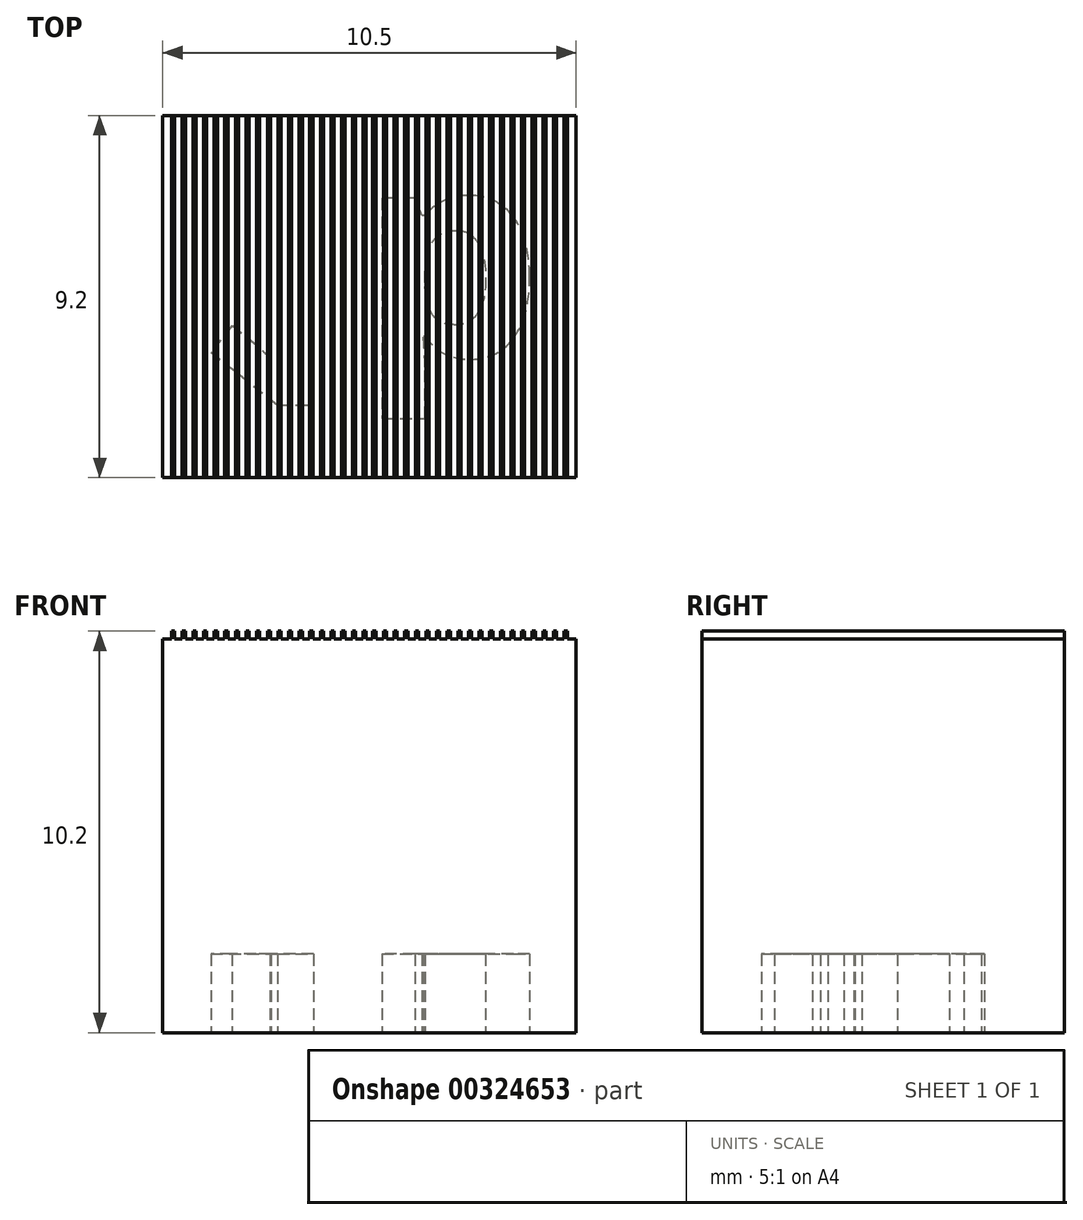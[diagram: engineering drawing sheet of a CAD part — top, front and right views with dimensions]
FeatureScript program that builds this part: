
annotation { "Feature Type Name" : "Feature", "Feature Type Description" : "" }
export const myFeature = defineFeature(function(context is Context, id is Id, definition is map)
    precondition{}
    {
        {
            assignVariable(context, id + "F0", {"name" : "h", "anyValue" : 10});
        }
        {
            assignVariable(context, id + "F1", {"name" : "gh", "anyValue" : 0.2});
        }
        {
            var Q0;
            Q0=qCreatedBy(makeId("Top.planeOp"),FACE);
            var sketch = newSketch(context, id + "F2", { "sketchPlane" : qUnion([Q0])});
            skLineSegment(sketch, "E0.bottom", {"start": v(5.25, 4.6) * mm, "end": v(-5.25, 4.6) * mm});
            skLineSegment(sketch, "E0.top", {"start": v(5.25, -4.6) * mm, "end": v(-5.25, -4.6) * mm});
            skLineSegment(sketch, "E0.left", {"start": v(5.25, 4.6) * mm, "end": v(5.25, -4.6) * mm});
            skLineSegment(sketch, "E0.right", {"start": v(-5.25, 4.6) * mm, "end": v(-5.25, -4.6) * mm});
            skPoint(sketch, "E0.middle", {"position": v(0, 0) * mm});
            skSolve(sketch);
        }
        {
            var Q0;
            Q0=qSketchRegion(id+"F2",true);
            extrude(context, id + "F3", {"entities" : qUnion([Q0]), "depth" : (getVariable(context, 'h')) * mm});
        }
        {
            var Q0;
            Q0=makeQuery(id+"F3.opExtrude","CAP_FACE",FACE,{"disambiguationData":[OSD([sQuery(id+"F2.wireOp",EDGE,"E0.bottom"),sQuery(id+"F2.wireOp",EDGE,"E0.top"),sQuery(id+"F2.wireOp",EDGE,"E0.left"),sQuery(id+"F2.wireOp",EDGE,"E0.right")])],"isStart":false});
            var sketch = newSketch(context, id + "F4", { "sketchPlane" : qUnion([Q0])});
            skLineSegment(sketch, "E1", {"start": v(0.08, 4.6) * mm, "end": v(0.09, -4.6) * mm});
            skLineSegment(sketch, "E2", {"start": v(-0.08, -4.6) * mm, "end": v(-0.09, 4.6) * mm, "construction": true});
            skLineSegment(sketch, "E3", {"start": v(0.17, -4.6) * mm, "end": v(0.16, 4.6) * mm});
            skLineSegment(sketch, "E4", {"start": v(0.09, 0) * mm, "end": v(-0.09, 0) * mm, "construction": true});
            skPoint(sketch, "E5", {"position": v(0, 0) * mm});
            skLineSegment(sketch, "E6", {"start": v(0.09, 4.6) * mm, "end": v(0.16, 4.6) * mm});
            skLineSegment(sketch, "E7", {"start": v(0.16, -4.6) * mm, "end": v(0.09, -4.6) * mm});
            skLineSegment(sketch, "E8.1.0.0", {"start": v(0.36, 4.6) * mm, "end": v(0.43, 4.6) * mm});
            skLineSegment(sketch, "E8.1.0.1", {"start": v(0.44, -4.6) * mm, "end": v(0.43, 4.6) * mm});
            skLineSegment(sketch, "E8.1.0.2", {"start": v(0.35, 4.6) * mm, "end": v(0.36, -4.6) * mm});
            skLineSegment(sketch, "E8.1.0.3", {"start": v(0.43, -4.6) * mm, "end": v(0.36, -4.6) * mm});
            skLineSegment(sketch, "E8.2.0.0", {"start": v(0.62, 4.6) * mm, "end": v(0.7, 4.6) * mm});
            skLineSegment(sketch, "E8.2.0.1", {"start": v(0.7, -4.6) * mm, "end": v(0.7, 4.6) * mm});
            skLineSegment(sketch, "E8.2.0.2", {"start": v(0.62, 4.6) * mm, "end": v(0.62, -4.6) * mm});
            skLineSegment(sketch, "E8.2.0.3", {"start": v(0.7, -4.6) * mm, "end": v(0.62, -4.6) * mm});
            skLineSegment(sketch, "E8.3.0.0", {"start": v(0.9, 4.6) * mm, "end": v(0.97, 4.6) * mm});
            skLineSegment(sketch, "E8.3.0.1", {"start": v(0.97, -4.6) * mm, "end": v(0.97, 4.6) * mm});
            skLineSegment(sketch, "E8.3.0.2", {"start": v(0.9, 4.6) * mm, "end": v(0.9, -4.6) * mm});
            skLineSegment(sketch, "E8.3.0.3", {"start": v(0.97, -4.6) * mm, "end": v(0.9, -4.6) * mm});
            skLineSegment(sketch, "E8.4.0.0", {"start": v(1.16, 4.6) * mm, "end": v(1.24, 4.6) * mm});
            skLineSegment(sketch, "E8.4.0.1", {"start": v(1.24, -4.6) * mm, "end": v(1.24, 4.6) * mm});
            skLineSegment(sketch, "E8.4.0.2", {"start": v(1.16, 4.6) * mm, "end": v(1.16, -4.6) * mm});
            skLineSegment(sketch, "E8.4.0.3", {"start": v(1.24, -4.6) * mm, "end": v(1.16, -4.6) * mm});
            skLineSegment(sketch, "E8.5.0.0", {"start": v(1.43, 4.6) * mm, "end": v(1.51, 4.6) * mm});
            skLineSegment(sketch, "E8.5.0.1", {"start": v(1.51, -4.6) * mm, "end": v(1.51, 4.6) * mm});
            skLineSegment(sketch, "E8.5.0.2", {"start": v(1.43, 4.6) * mm, "end": v(1.43, -4.6) * mm});
            skLineSegment(sketch, "E8.5.0.3", {"start": v(1.51, -4.6) * mm, "end": v(1.43, -4.6) * mm});
            skLineSegment(sketch, "E8.6.0.0", {"start": v(1.7, 4.6) * mm, "end": v(1.78, 4.6) * mm});
            skLineSegment(sketch, "E8.6.0.1", {"start": v(1.78, -4.6) * mm, "end": v(1.78, 4.6) * mm});
            skLineSegment(sketch, "E8.6.0.2", {"start": v(1.7, 4.6) * mm, "end": v(1.7, -4.6) * mm});
            skLineSegment(sketch, "E8.6.0.3", {"start": v(1.78, -4.6) * mm, "end": v(1.7, -4.6) * mm});
            skLineSegment(sketch, "E8.7.0.0", {"start": v(1.97, 4.6) * mm, "end": v(2.05, 4.6) * mm});
            skLineSegment(sketch, "E8.7.0.1", {"start": v(2.05, -4.6) * mm, "end": v(2.05, 4.6) * mm});
            skLineSegment(sketch, "E8.7.0.2", {"start": v(1.97, 4.6) * mm, "end": v(1.97, -4.6) * mm});
            skLineSegment(sketch, "E8.7.0.3", {"start": v(2.05, -4.6) * mm, "end": v(1.97, -4.6) * mm});
            skLineSegment(sketch, "E8.8.0.0", {"start": v(2.24, 4.6) * mm, "end": v(2.32, 4.6) * mm});
            skLineSegment(sketch, "E8.8.0.1", {"start": v(2.32, -4.6) * mm, "end": v(2.32, 4.6) * mm});
            skLineSegment(sketch, "E8.8.0.2", {"start": v(2.24, 4.6) * mm, "end": v(2.24, -4.6) * mm});
            skLineSegment(sketch, "E8.8.0.3", {"start": v(2.32, -4.6) * mm, "end": v(2.24, -4.6) * mm});
            skLineSegment(sketch, "E8.9.0.0", {"start": v(2.51, 4.6) * mm, "end": v(2.6, 4.6) * mm});
            skLineSegment(sketch, "E8.9.0.1", {"start": v(2.6, -4.6) * mm, "end": v(2.6, 4.6) * mm});
            skLineSegment(sketch, "E8.9.0.2", {"start": v(2.51, 4.6) * mm, "end": v(2.51, -4.6) * mm});
            skLineSegment(sketch, "E8.9.0.3", {"start": v(2.6, -4.6) * mm, "end": v(2.51, -4.6) * mm});
            skLineSegment(sketch, "E8.direction1", {"start": v(0.09, 4.6) * mm, "end": v(0.36, 4.6) * mm, "construction": true});
            skLineSegment(sketch, "E9.0.10.0", {"start": v(2.78, 4.6) * mm, "end": v(2.86, 4.6) * mm});
            skLineSegment(sketch, "E9.3.10.0", {"start": v(2.86, -4.6) * mm, "end": v(2.86, 4.6) * mm});
            skLineSegment(sketch, "E9.6.10.0", {"start": v(2.78, 4.6) * mm, "end": v(2.78, -4.6) * mm});
            skLineSegment(sketch, "E9.9.10.0", {"start": v(2.86, -4.6) * mm, "end": v(2.78, -4.6) * mm});
            skLineSegment(sketch, "E10.0.11.0", {"start": v(3.05, 4.6) * mm, "end": v(3.13, 4.6) * mm});
            skLineSegment(sketch, "E10.3.11.0", {"start": v(3.13, -4.6) * mm, "end": v(3.13, 4.6) * mm});
            skLineSegment(sketch, "E10.6.11.0", {"start": v(3.05, 4.6) * mm, "end": v(3.05, -4.6) * mm});
            skLineSegment(sketch, "E10.9.11.0", {"start": v(3.13, -4.6) * mm, "end": v(3.05, -4.6) * mm});
            skLineSegment(sketch, "E11.0.12.0", {"start": v(3.32, 4.6) * mm, "end": v(3.4, 4.6) * mm});
            skLineSegment(sketch, "E11.3.12.0", {"start": v(3.4, -4.6) * mm, "end": v(3.4, 4.6) * mm});
            skLineSegment(sketch, "E11.6.12.0", {"start": v(3.32, 4.6) * mm, "end": v(3.32, -4.6) * mm});
            skLineSegment(sketch, "E11.9.12.0", {"start": v(3.4, -4.6) * mm, "end": v(3.32, -4.6) * mm});
            skLineSegment(sketch, "E12.0.13.0", {"start": v(3.6, 4.6) * mm, "end": v(3.67, 4.6) * mm});
            skLineSegment(sketch, "E12.3.13.0", {"start": v(3.67, -4.6) * mm, "end": v(3.67, 4.6) * mm});
            skLineSegment(sketch, "E12.6.13.0", {"start": v(3.6, 4.6) * mm, "end": v(3.6, -4.6) * mm});
            skLineSegment(sketch, "E12.9.13.0", {"start": v(3.67, -4.6) * mm, "end": v(3.6, -4.6) * mm});
            skLineSegment(sketch, "E13.0.14.0", {"start": v(3.86, 4.6) * mm, "end": v(3.94, 4.6) * mm});
            skLineSegment(sketch, "E13.3.14.0", {"start": v(3.94, -4.6) * mm, "end": v(3.94, 4.6) * mm});
            skLineSegment(sketch, "E13.6.14.0", {"start": v(3.86, 4.6) * mm, "end": v(3.86, -4.6) * mm});
            skLineSegment(sketch, "E13.9.14.0", {"start": v(3.94, -4.6) * mm, "end": v(3.86, -4.6) * mm});
            skLineSegment(sketch, "E14.0.15.0", {"start": v(4.13, 4.6) * mm, "end": v(4.21, 4.6) * mm});
            skLineSegment(sketch, "E14.3.15.0", {"start": v(4.21, -4.6) * mm, "end": v(4.21, 4.6) * mm});
            skLineSegment(sketch, "E14.6.15.0", {"start": v(4.13, 4.6) * mm, "end": v(4.13, -4.6) * mm});
            skLineSegment(sketch, "E14.9.15.0", {"start": v(4.21, -4.6) * mm, "end": v(4.13, -4.6) * mm});
            skLineSegment(sketch, "E14.0.16.0", {"start": v(4.4, 4.6) * mm, "end": v(4.48, 4.6) * mm});
            skLineSegment(sketch, "E14.3.16.0", {"start": v(4.48, -4.6) * mm, "end": v(4.48, 4.6) * mm});
            skLineSegment(sketch, "E14.6.16.0", {"start": v(4.4, 4.6) * mm, "end": v(4.4, -4.6) * mm});
            skLineSegment(sketch, "E14.9.16.0", {"start": v(4.48, -4.6) * mm, "end": v(4.4, -4.6) * mm});
            skLineSegment(sketch, "E15.0.17.0", {"start": v(4.67, 4.6) * mm, "end": v(4.75, 4.6) * mm});
            skLineSegment(sketch, "E15.3.17.0", {"start": v(4.75, -4.6) * mm, "end": v(4.75, 4.6) * mm});
            skLineSegment(sketch, "E15.6.17.0", {"start": v(4.67, 4.6) * mm, "end": v(4.67, -4.6) * mm});
            skLineSegment(sketch, "E15.9.17.0", {"start": v(4.75, -4.6) * mm, "end": v(4.67, -4.6) * mm});
            skLineSegment(sketch, "E15.0.18.0", {"start": v(4.94, 4.6) * mm, "end": v(5.02, 4.6) * mm});
            skLineSegment(sketch, "E15.3.18.0", {"start": v(5.02, -4.6) * mm, "end": v(5.02, 4.6) * mm});
            skLineSegment(sketch, "E15.6.18.0", {"start": v(4.94, 4.6) * mm, "end": v(4.94, -4.6) * mm});
            skLineSegment(sketch, "E15.9.18.0", {"start": v(5.02, -4.6) * mm, "end": v(4.94, -4.6) * mm});
            skLineSegment(sketch, "E16.MirrorCS", {"start": v(-0.36, 4.6) * mm, "end": v(-0.43, 4.6) * mm});
            skLineSegment(sketch, "E17.MirrorCS", {"start": v(-0.09, 4.6) * mm, "end": v(-0.16, 4.6) * mm});
            skLineSegment(sketch, "E18.MirrorCS", {"start": v(-4.67, 4.6) * mm, "end": v(-4.75, 4.6) * mm});
            skLineSegment(sketch, "E19.MirrorCS", {"start": v(-2.6, -4.6) * mm, "end": v(-2.51, -4.6) * mm});
            skLineSegment(sketch, "E20.MirrorCS", {"start": v(-3.6, 4.6) * mm, "end": v(-3.67, 4.6) * mm});
            skLineSegment(sketch, "E21.MirrorCS", {"start": v(-1.7, 4.6) * mm, "end": v(-1.78, 4.6) * mm});
            skLineSegment(sketch, "E22.MirrorCS", {"start": v(-2.05, -4.6) * mm, "end": v(-1.97, -4.6) * mm});
            skLineSegment(sketch, "E23.MirrorCS", {"start": v(-1.51, -4.6) * mm, "end": v(-1.43, -4.6) * mm});
            skLineSegment(sketch, "E24.MirrorCS", {"start": v(-5.02, -4.6) * mm, "end": v(-4.94, -4.6) * mm});
            skLineSegment(sketch, "E25.MirrorCS", {"start": v(-3.32, 4.6) * mm, "end": v(-3.4, 4.6) * mm});
            skLineSegment(sketch, "E26.MirrorCS", {"start": v(-0.9, 4.6) * mm, "end": v(-0.97, 4.6) * mm});
            skLineSegment(sketch, "E27.MirrorCS", {"start": v(-1.97, 4.6) * mm, "end": v(-2.05, 4.6) * mm});
            skLineSegment(sketch, "E28.MirrorCS", {"start": v(-4.4, 4.6) * mm, "end": v(-4.48, 4.6) * mm});
            skLineSegment(sketch, "E29.MirrorCS", {"start": v(-0.16, -4.6) * mm, "end": v(-0.09, -4.6) * mm});
            skLineSegment(sketch, "E30.MirrorCS", {"start": v(-4.94, 4.6) * mm, "end": v(-5.02, 4.6) * mm});
            skLineSegment(sketch, "E31.MirrorCS", {"start": v(-2.78, 4.6) * mm, "end": v(-2.86, 4.6) * mm});
            skLineSegment(sketch, "E32.MirrorCS", {"start": v(-3.86, 4.6) * mm, "end": v(-3.94, 4.6) * mm});
            skLineSegment(sketch, "E33.MirrorCS", {"start": v(-3.13, -4.6) * mm, "end": v(-3.05, -4.6) * mm});
            skLineSegment(sketch, "E34.MirrorCS", {"start": v(-4.21, -4.6) * mm, "end": v(-4.13, -4.6) * mm});
            skLineSegment(sketch, "E35.MirrorCS", {"start": v(-1.16, 4.6) * mm, "end": v(-1.24, 4.6) * mm});
            skLineSegment(sketch, "E36.MirrorCS", {"start": v(-4.48, -4.6) * mm, "end": v(-4.4, -4.6) * mm});
            skLineSegment(sketch, "E37.MirrorCS", {"start": v(-3.4, -4.6) * mm, "end": v(-3.32, -4.6) * mm});
            skLineSegment(sketch, "E38.MirrorCS", {"start": v(-1.43, 4.6) * mm, "end": v(-1.51, 4.6) * mm});
            skLineSegment(sketch, "E39.MirrorCS", {"start": v(-2.51, 4.6) * mm, "end": v(-2.6, 4.6) * mm});
            skLineSegment(sketch, "E40.MirrorCS", {"start": v(-1.24, -4.6) * mm, "end": v(-1.16, -4.6) * mm});
            skLineSegment(sketch, "E41.MirrorCS", {"start": v(-2.24, 4.6) * mm, "end": v(-2.32, 4.6) * mm});
            skLineSegment(sketch, "E42.MirrorCS", {"start": v(-0.97, -4.6) * mm, "end": v(-0.9, -4.6) * mm});
            skLineSegment(sketch, "E43.MirrorCS", {"start": v(-1.78, -4.6) * mm, "end": v(-1.7, -4.6) * mm});
            skLineSegment(sketch, "E44.MirrorCS", {"start": v(-0.7, -4.6) * mm, "end": v(-0.62, -4.6) * mm});
            skLineSegment(sketch, "E45.MirrorCS", {"start": v(-4.75, -4.6) * mm, "end": v(-4.67, -4.6) * mm});
            skLineSegment(sketch, "E46.MirrorCS", {"start": v(-3.67, -4.6) * mm, "end": v(-3.6, -4.6) * mm});
            skLineSegment(sketch, "E47.MirrorCS", {"start": v(-0.09, 4.6) * mm, "end": v(-0.36, 4.6) * mm, "construction": true});
            skLineSegment(sketch, "E48.MirrorCS", {"start": v(-0.43, -4.6) * mm, "end": v(-0.36, -4.6) * mm});
            skLineSegment(sketch, "E49.MirrorCS", {"start": v(-0.62, 4.6) * mm, "end": v(-0.7, 4.6) * mm});
            skLineSegment(sketch, "E50.MirrorCS", {"start": v(-3.94, -4.6) * mm, "end": v(-3.86, -4.6) * mm});
            skLineSegment(sketch, "E51.MirrorCS", {"start": v(-2.86, -4.6) * mm, "end": v(-2.78, -4.6) * mm});
            skLineSegment(sketch, "E52.MirrorCS", {"start": v(-2.32, -4.6) * mm, "end": v(-2.24, -4.6) * mm});
            skLineSegment(sketch, "E53.MirrorCS", {"start": v(-4.13, 4.6) * mm, "end": v(-4.21, 4.6) * mm});
            skLineSegment(sketch, "E54.MirrorCS", {"start": v(-0.09, 0) * mm, "end": v(0.09, 0) * mm, "construction": true});
            skLineSegment(sketch, "E55.MirrorCS", {"start": v(-3.05, 4.6) * mm, "end": v(-3.13, 4.6) * mm});
            skLineSegment(sketch, "E56.MirrorCS", {"start": v(-4.67, 4.6) * mm, "end": v(-4.67, -4.6) * mm});
            skLineSegment(sketch, "E57.MirrorCS", {"start": v(-3.6, 4.6) * mm, "end": v(-3.6, -4.6) * mm});
            skLineSegment(sketch, "E58.MirrorCS", {"start": v(-4.21, -4.6) * mm, "end": v(-4.21, 4.6) * mm});
            skLineSegment(sketch, "E59.MirrorCS", {"start": v(-3.13, -4.6) * mm, "end": v(-3.13, 4.6) * mm});
            skLineSegment(sketch, "E60.MirrorCS", {"start": v(-2.6, -4.6) * mm, "end": v(-2.6, 4.6) * mm});
            skLineSegment(sketch, "E61.MirrorCS", {"start": v(-4.75, -4.6) * mm, "end": v(-4.75, 4.6) * mm});
            skLineSegment(sketch, "E62.MirrorCS", {"start": v(-3.67, -4.6) * mm, "end": v(-3.67, 4.6) * mm});
            skLineSegment(sketch, "E63.MirrorCS", {"start": v(-2.51, 4.6) * mm, "end": v(-2.51, -4.6) * mm});
            skLineSegment(sketch, "E64.MirrorCS", {"start": v(-1.43, 4.6) * mm, "end": v(-1.43, -4.6) * mm});
            skLineSegment(sketch, "E65.MirrorCS", {"start": v(-1.7, 4.6) * mm, "end": v(-1.7, -4.6) * mm});
            skLineSegment(sketch, "E66.MirrorCS", {"start": v(-0.62, 4.6) * mm, "end": v(-0.62, -4.6) * mm});
            skLineSegment(sketch, "E67.MirrorCS", {"start": v(-1.24, -4.6) * mm, "end": v(-1.24, 4.6) * mm});
            skLineSegment(sketch, "E68.MirrorCS", {"start": v(-2.32, -4.6) * mm, "end": v(-2.32, 4.6) * mm});
            skLineSegment(sketch, "E69.MirrorCS", {"start": v(-1.97, 4.6) * mm, "end": v(-1.97, -4.6) * mm});
            skLineSegment(sketch, "E70.MirrorCS", {"start": v(-2.86, -4.6) * mm, "end": v(-2.86, 4.6) * mm});
            skLineSegment(sketch, "E71.MirrorCS", {"start": v(-0.08, 4.6) * mm, "end": v(-0.08, -4.6) * mm});
            skLineSegment(sketch, "E72.MirrorCS", {"start": v(-3.94, -4.6) * mm, "end": v(-3.94, 4.6) * mm});
            skLineSegment(sketch, "E73.MirrorCS", {"start": v(-0.16, -4.6) * mm, "end": v(-0.17, 4.6) * mm});
            skLineSegment(sketch, "E74.MirrorCS", {"start": v(-0.35, 4.6) * mm, "end": v(-0.35, -4.6) * mm});
            skLineSegment(sketch, "E75.MirrorCS", {"start": v(-1.78, -4.6) * mm, "end": v(-1.78, 4.6) * mm});
            skLineSegment(sketch, "E76.MirrorCS", {"start": v(-2.05, -4.6) * mm, "end": v(-2.05, 4.6) * mm});
            skLineSegment(sketch, "E77.MirrorCS", {"start": v(-0.97, -4.6) * mm, "end": v(-0.97, 4.6) * mm});
            skLineSegment(sketch, "E78.MirrorCS", {"start": v(-4.4, 4.6) * mm, "end": v(-4.4, -4.6) * mm});
            skLineSegment(sketch, "E79.MirrorCS", {"start": v(-0.43, -4.6) * mm, "end": v(-0.43, 4.6) * mm});
            skLineSegment(sketch, "E80.MirrorCS", {"start": v(-3.32, 4.6) * mm, "end": v(-3.32, -4.6) * mm});
            skLineSegment(sketch, "E81.MirrorCS", {"start": v(-4.48, -4.6) * mm, "end": v(-4.48, 4.6) * mm});
            skLineSegment(sketch, "E82.MirrorCS", {"start": v(-3.4, -4.6) * mm, "end": v(-3.4, 4.6) * mm});
            skLineSegment(sketch, "E83.MirrorCS", {"start": v(-2.24, 4.6) * mm, "end": v(-2.24, -4.6) * mm});
            skLineSegment(sketch, "E84.MirrorCS", {"start": v(0.09, -4.6) * mm, "end": v(0.08, 4.6) * mm, "construction": true});
            skLineSegment(sketch, "E85.MirrorCS", {"start": v(-1.16, 4.6) * mm, "end": v(-1.16, -4.6) * mm});
            skLineSegment(sketch, "E86.MirrorCS", {"start": v(-4.13, 4.6) * mm, "end": v(-4.13, -4.6) * mm});
            skLineSegment(sketch, "E87.MirrorCS", {"start": v(-3.05, 4.6) * mm, "end": v(-3.05, -4.6) * mm});
            skLineSegment(sketch, "E88.MirrorCS", {"start": v(-4.94, 4.6) * mm, "end": v(-4.94, -4.6) * mm});
            skLineSegment(sketch, "E89.MirrorCS", {"start": v(-3.86, 4.6) * mm, "end": v(-3.86, -4.6) * mm});
            skLineSegment(sketch, "E90.MirrorCS", {"start": v(-2.78, 4.6) * mm, "end": v(-2.78, -4.6) * mm});
            skLineSegment(sketch, "E91.MirrorCS", {"start": v(-0.9, 4.6) * mm, "end": v(-0.9, -4.6) * mm});
            skLineSegment(sketch, "E92.MirrorCS", {"start": v(-0.7, -4.6) * mm, "end": v(-0.7, 4.6) * mm});
            skLineSegment(sketch, "E93.MirrorCS", {"start": v(-5.02, -4.6) * mm, "end": v(-5.02, 4.6) * mm});
            skLineSegment(sketch, "E94.MirrorCS", {"start": v(-1.51, -4.6) * mm, "end": v(-1.51, 4.6) * mm});
            skSolve(sketch);
        }
        {
            var Q0;
            Q0=qSketchRegion(id+"F4",true);
            extrude(context, id + "F5", {"entities" : qUnion([Q0]), "operationType" : NewBodyOperationType.ADD, "depth" : (getVariable(context, 'gh')) * mm});
        }
        {
            var Q0;
            Q0=makeQuery(id+"F3.opExtrude","CAP_FACE",FACE,{"disambiguationData":[OSD([sQuery(id+"F2.wireOp",EDGE,"E0.bottom"),sQuery(id+"F2.wireOp",EDGE,"E0.top"),sQuery(id+"F2.wireOp",EDGE,"E0.left"),sQuery(id+"F2.wireOp",EDGE,"E0.right")])],"isStart":true});
            var sketch = newSketch(context, id + "F6", { "sketchPlane" : qUnion([Q0])});
            skText(sketch, "E95", { "text": "1b", "fontName": "OpenSans-Bold.ttf"});
            const initialGuessF6  = {"E95": [-0.00446, -0.0025, 1, 0, 0.0053]};
            skSetInitialGuess(sketch, initialGuessF6);
            skSolve(sketch);
        }
        {
            var Q0;
            Q0=qSketchRegion(id+"F6",true);
            extrude(context, id + "F7", {"entities" : qUnion([Q0]), "operationType" : NewBodyOperationType.REMOVE, "oppositeDirection" : true, "depth" : 2 * mm});
        }
    });
